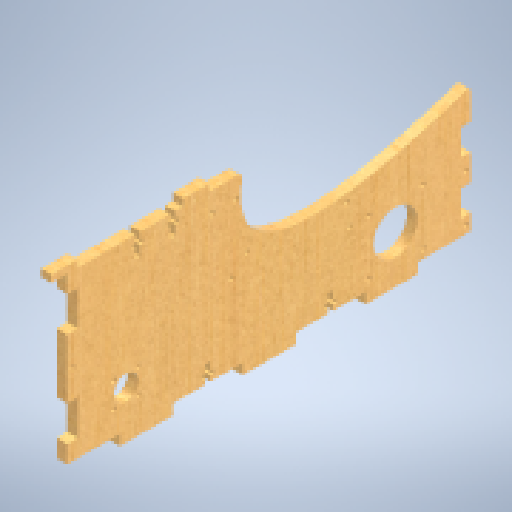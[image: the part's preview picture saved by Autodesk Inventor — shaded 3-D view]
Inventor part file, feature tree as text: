
AUTODESK INVENTOR PART (.ipt)
format: ipt  version: 2024.2 (Build 282272000, 272)  size: 721,408 bytes
history: native  units: mm
features: extrude x14, sketch x14, other x4, fillet x1, reference x1
ambient origin geometry x8: Origin, YZ Plane, XZ Plane, XY Plane, X Axis, Y Axis, Z Axis, Center Point
bodies: Body1 (feature_tree)
feature tree (34):
  other  "Твердое тело1"
  extrude  "Выдавливание1"  Depth=230.0mm
  extrude  "Выдавливание2"  Depth=100.0mm
  extrude  "Выдавливание3"  Depth=6.0mm TaperAngle=0.0deg
  extrude  "Выдавливание4"  Depth=30.0mm
  extrude  "Выдавливание5"  Depth=30.0mm
  extrude  "Выдавливание6"  Depth=40.0mm
  extrude  "Выдавливание7"  Depth=30.0mm
  extrude  "Выдавливание8"  Depth=30.0mm
  extrude  "Выдавливание9"  Depth=40.0mm
  fillet  "Сопряжение1"  [1 undecoded]
  extrude  "Выдавливание11"  Depth=6.0mm
  extrude  "Выдавливание12"  Depth=6.0mm
  extrude  "Выдавливание13"  Depth=10.0mm
  extrude  "Выдавливание14"  Depth=10.0mm
  extrude  "Выдавливание10"  Depth=20.0mm
  sketch  "Эскиз1"
  sketch  "Эскиз2"
  sketch  "Эскиз3"
  sketch  "Эскиз4"
  sketch  "Эскиз5"
  sketch  "Эскиз6"
  sketch  "Эскиз7"
  sketch  "Эскиз8"
  sketch  "Эскиз9"
  sketch  "Эскиз10"
  sketch  "Эскиз11"
  sketch  "Эскиз12"
  reference  "Ссылка1"
  sketch  "Эскиз13"
  sketch  "Эскиз14"
  other  "<userpath>\Documents\Artist-v2\3D\Робот.iam"
  other  "Робот.iam"
  other  "крышка:1"
note: 1 required parameter value undecoded (feature->parameter linkage not recoverable at this tier; creation-order binding heuristic only, values carry confidence <= 0.55)
